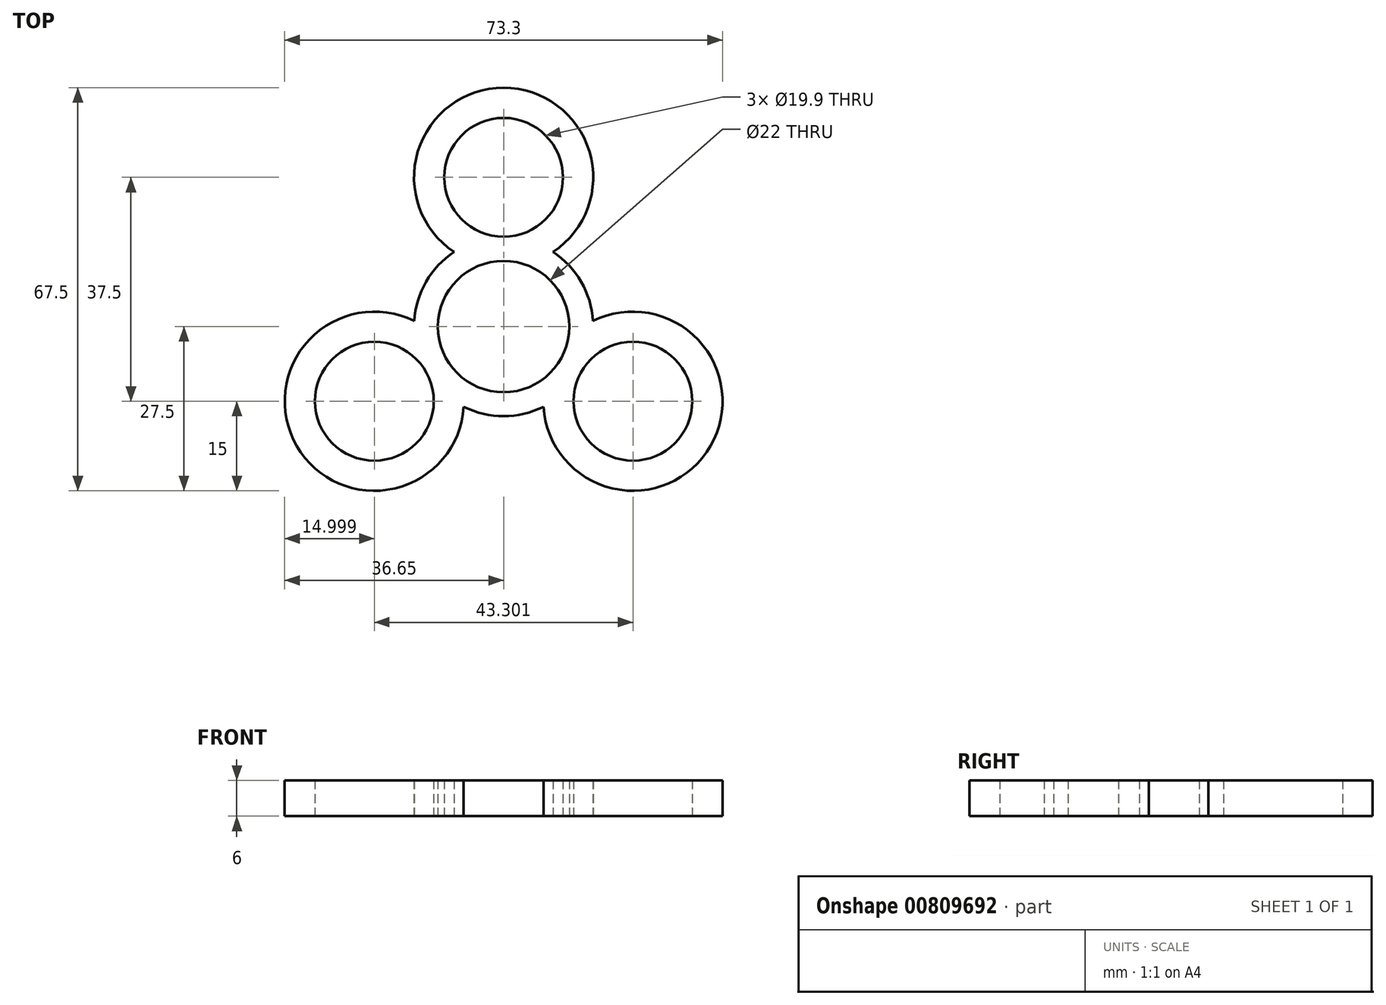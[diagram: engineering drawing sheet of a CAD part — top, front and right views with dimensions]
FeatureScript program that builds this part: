
annotation { "Feature Type Name" : "Feature", "Feature Type Description" : "" }
export const myFeature = defineFeature(function(context is Context, id is Id, definition is map)
    precondition{}
    {
        {
            var Q0;
            Q0=qCreatedBy(makeId("Top.planeOp"),FACE);
            var sketch = newSketch(context, id + "F0", { "sketchPlane" : qUnion([Q0])});
            skArc(sketch, "E0", {"start": v(9.53, 5.5) * mm, "mid": v(0, 11) * mm, "end": v(-9.53, 5.5) * mm});
            skCircle(sketch, "E1", {"center": v(0, 25) * mm, "radius": 9.95 * mm});
            skArc(sketch, "E2", {"start": v(13, 7.5) * mm, "mid": v(10.93, 10.27) * mm, "end": v(8.3, 12.5) * mm});
            skLineSegment(sketch, "E3", {"start": v(0, 0) * mm, "end": v(-13, 7.5) * mm});
            skLineSegment(sketch, "E4", {"start": v(-13, 7.5) * mm, "end": v(0, 0) * mm});
            skLineSegment(sketch, "E5", {"start": v(0, 0) * mm, "end": v(13, 7.5) * mm});
            skArc(sketch, "E6.trimOffspring", {"start": v(-8.3, 12.5) * mm, "mid": v(-10.93, 10.27) * mm, "end": v(-13, 7.5) * mm});
            skArc(sketch, "E7.trimOffspring", {"start": v(8.3, 12.5) * mm, "mid": v(0, 40) * mm, "end": v(-8.3, 12.5) * mm});
            skArc(sketch, "E8.1.1", {"start": v(-14.97, 0.93) * mm, "mid": v(-34.64, -20) * mm, "end": v(-6.68, -13.43) * mm});
            skCircle(sketch, "E8.1.2", {"center": v(-21.65, -12.5) * mm, "radius": 9.95 * mm});
            skArc(sketch, "E8.1.3", {"start": v(-9.53, 5.5) * mm, "mid": v(-9.53, -5.5) * mm, "end": v(0, -11) * mm});
            skArc(sketch, "E8.1.4", {"start": v(-6.68, -13.43) * mm, "mid": v(-3.43, -14.6) * mm, "end": v(0, -15) * mm});
            skArc(sketch, "E8.1.5", {"start": v(-13, 7.5) * mm, "mid": v(-14.36, 4.33) * mm, "end": v(-14.97, 0.93) * mm});
            skArc(sketch, "E8.2.1", {"start": v(6.68, -13.43) * mm, "mid": v(34.64, -20) * mm, "end": v(14.97, 0.93) * mm});
            skCircle(sketch, "E8.2.2", {"center": v(21.65, -12.5) * mm, "radius": 9.95 * mm});
            skArc(sketch, "E8.2.3", {"start": v(0, -11) * mm, "mid": v(9.53, -5.5) * mm, "end": v(9.53, 5.5) * mm});
            skArc(sketch, "E8.2.4", {"start": v(14.97, 0.93) * mm, "mid": v(14.36, 4.33) * mm, "end": v(13, 7.5) * mm});
            skArc(sketch, "E8.2.5", {"start": v(0, -15) * mm, "mid": v(3.43, -14.6) * mm, "end": v(6.68, -13.43) * mm});
            skSolve(sketch);
        }
        {
            var Q0;
            Q0 = qSketchRegion(id + "F0", true);
            extrude(context, id + "F1", {"entities" : qUnion([Q0]), "depth" : 6 * mm, "offsetDistance" : 25 * mm});
        }
    });
